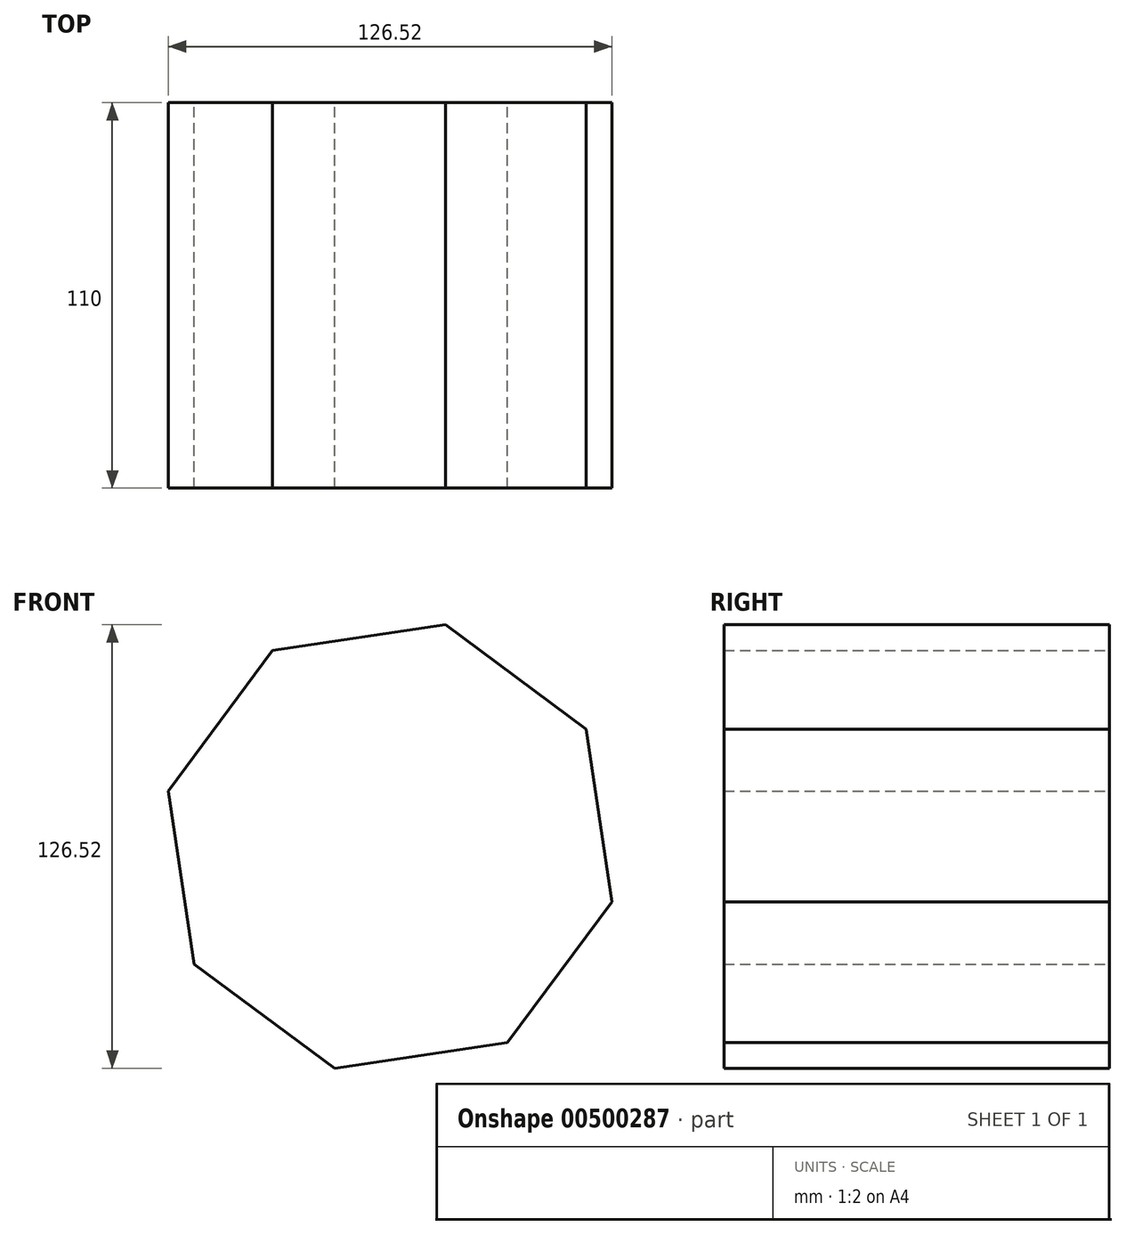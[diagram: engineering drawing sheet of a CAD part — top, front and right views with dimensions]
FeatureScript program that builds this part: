
annotation { "Feature Type Name" : "Feature", "Feature Type Description" : "" }
export const myFeature = defineFeature(function(context is Context, id is Id, definition is map)
    precondition{}
    {
        {
            var Q0;
            Q0=qCreatedBy(makeId("Front.planeOp"),FACE);
            var sketch = newSketch(context, id + "F0", { "sketchPlane" : qUnion([Q0])});
            skCircle(sketch, "E0.cCircle", {"center": v(0, 0) * mm, "radius": 65.21 * mm, "construction": true});
            skLineSegment(sketch, "E0.0", {"start": v(-33.53, 55.93) * mm, "end": v(15.84, 63.26) * mm});
            skLineSegment(sketch, "E0.1", {"start": v(15.84, 63.26) * mm, "end": v(55.93, 33.53) * mm});
            skLineSegment(sketch, "E0.2", {"start": v(55.93, 33.53) * mm, "end": v(63.26, -15.84) * mm});
            skLineSegment(sketch, "E0.3", {"start": v(63.26, -15.84) * mm, "end": v(33.53, -55.93) * mm});
            skLineSegment(sketch, "E0.4", {"start": v(33.53, -55.93) * mm, "end": v(-15.84, -63.26) * mm});
            skLineSegment(sketch, "E0.5", {"start": v(-15.84, -63.26) * mm, "end": v(-55.93, -33.53) * mm});
            skLineSegment(sketch, "E0.6", {"start": v(-55.93, -33.53) * mm, "end": v(-63.26, 15.84) * mm});
            skLineSegment(sketch, "E0.7", {"start": v(-63.26, 15.84) * mm, "end": v(-33.53, 55.93) * mm});
            skSolve(sketch);
        }
        {
            var Q0;
            Q0=makeQuery(id+"F0.imprint","IMPRINT",FACE,{"disambiguationData":[TD([[makeQuery(id+"F0.imprint","IMPRINT",EDGE,{"derivedFrom":sQuery(id+"F0.wireOp",EDGE,"E0.0")}),-1.0]])]});
            extrude(context, id + "F1", {"entities" : qUnion([Q0]), "depth" : 110 * mm});
        }
    });
